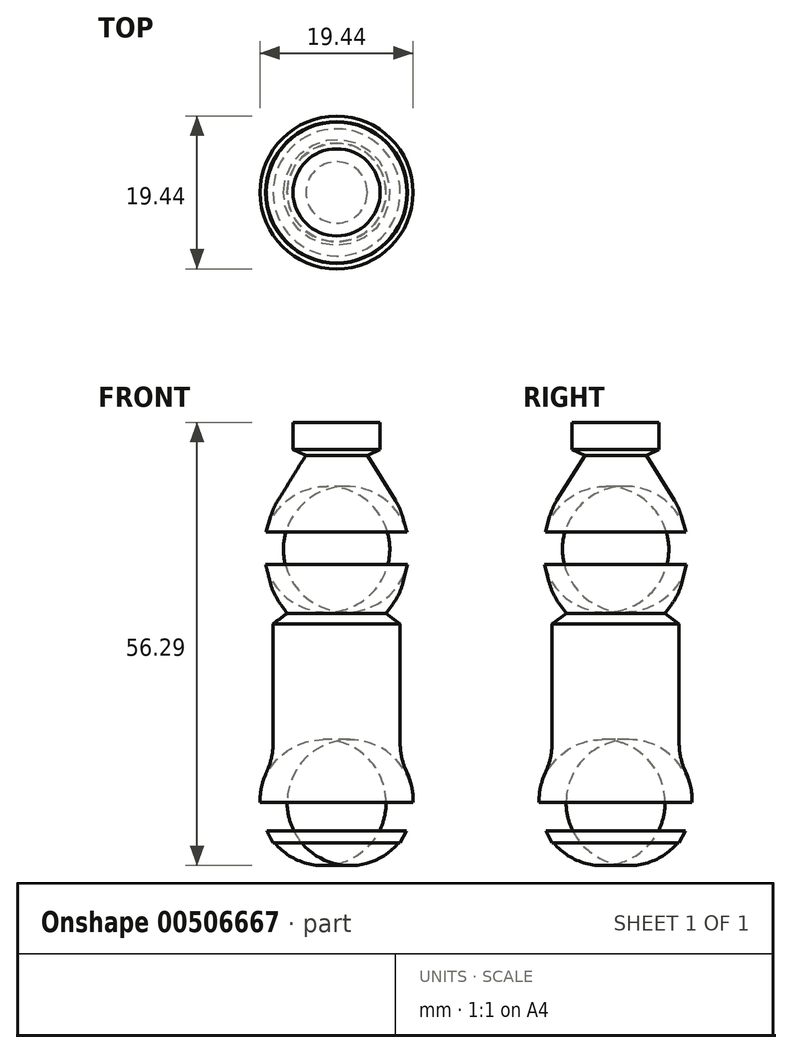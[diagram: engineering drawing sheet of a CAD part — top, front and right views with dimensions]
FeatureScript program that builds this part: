
annotation { "Feature Type Name" : "Feature", "Feature Type Description" : "" }
export const myFeature = defineFeature(function(context is Context, id is Id, definition is map)
    precondition{}
    {
        {
            var Q0;
            Q0=qCreatedBy(makeId("Front.planeOp"),FACE);
            var sketch = newSketch(context, id + "F0", { "sketchPlane" : qUnion([Q0])});
            skLineSegment(sketch, "E0", {"start": v(0, 53.44) * mm, "end": v(5.53, 53.44) * mm});
            skLineSegment(sketch, "E1", {"start": v(3.9, 49.26) * mm, "end": v(8.07, 42.55) * mm});
            skLineSegment(sketch, "E2", {"start": v(8.07, 42.55) * mm, "end": v(9.53, 37.47) * mm});
            skLineSegment(sketch, "E3", {"start": v(9.53, 37.47) * mm, "end": v(8.07, 31.66) * mm});
            skLineSegment(sketch, "E4", {"start": v(8.07, 31.66) * mm, "end": v(6.27, 29.19) * mm});
            skLineSegment(sketch, "E5", {"start": v(6.27, 29.19) * mm, "end": v(8.07, 27.87) * mm});
            skLineSegment(sketch, "E6", {"start": v(8.07, 27.87) * mm, "end": v(8.07, 11.04) * mm});
            skLineSegment(sketch, "E7", {"start": v(8.07, 11.04) * mm, "end": v(9.72, 7.05) * mm});
            skLineSegment(sketch, "E8", {"start": v(9.72, 7.05) * mm, "end": v(9.72, 3.24) * mm});
            skLineSegment(sketch, "E9", {"start": v(9.72, 3.24) * mm, "end": v(8.07, 0) * mm});
            skLineSegment(sketch, "E10", {"start": v(8.07, 0) * mm, "end": v(0, 0) * mm});
            skLineSegment(sketch, "E11", {"start": v(0, 0) * mm, "end": v(0, 53.44) * mm});
            skLineSegment(sketch, "E12", {"start": v(5.53, 53.44) * mm, "end": v(5.53, 49.99) * mm});
            skLineSegment(sketch, "E13", {"start": v(5.53, 49.99) * mm, "end": v(3.9, 49.26) * mm});
            skSolve(sketch);
        }
        {
            var Q0;
            Q0 = qSketchRegion(id + "F0", true);
            var Q1;
            Q1=sQuery(id+"F0.wireOp",EDGE,"E11");
            revolve(context, id + "F1", {"entities" : qUnion([Q0]), "axis" : qUnion([Q1]), "revolveType" : RevolveType.FULL});
        }
        {
            var Q0;
            Q0=makeQuery(id+"F1.opRevolve","SWEPT_EDGE",EDGE,{"disambiguationData":[OSD([sQuery(id+"F0.wireOp",EDGE,"E1"),sQuery(id+"F0.wireOp",EDGE,"E2")])]});
            var Q1;
            Q1=makeQuery(id+"F1.opRevolve","SWEPT_EDGE",EDGE,{"disambiguationData":[OSD([sQuery(id+"F0.wireOp",EDGE,"E2"),sQuery(id+"F0.wireOp",EDGE,"E3")])]});
            var Q2;
            Q2=makeQuery(id+"F1.opRevolve","SWEPT_EDGE",EDGE,{"disambiguationData":[OSD([sQuery(id+"F0.wireOp",EDGE,"E3"),sQuery(id+"F0.wireOp",EDGE,"E4")])]});
            fillet(context, id + "F2", {"entities" : qUnion([Q0, Q1, Q2]), "radius" : 8 * mm, "tangentPropagation" : true, "allowEdgeOverflow" : false});
        }
        {
            var Q0;
            Q0=makeQuery(id+"F1.opRevolve","SWEPT_EDGE",EDGE,{"disambiguationData":[OSD([sQuery(id+"F0.wireOp",EDGE,"E6"),sQuery(id+"F0.wireOp",EDGE,"E7")])]});
            var Q1;
            Q1=makeQuery(id+"F1.opRevolve","SWEPT_EDGE",EDGE,{"disambiguationData":[OSD([sQuery(id+"F0.wireOp",EDGE,"E7"),sQuery(id+"F0.wireOp",EDGE,"E8")])]});
            var Q2;
            Q2=makeQuery(id+"F1.opRevolve","SWEPT_EDGE",EDGE,{"disambiguationData":[OSD([sQuery(id+"F0.wireOp",EDGE,"E8"),sQuery(id+"F0.wireOp",EDGE,"E9")])]});
            fillet(context, id + "F3", {"entities" : qUnion([Q0, Q1, Q2]), "radius" : 8 * mm, "tangentPropagation" : true, "allowEdgeOverflow" : false});
        }
    });
